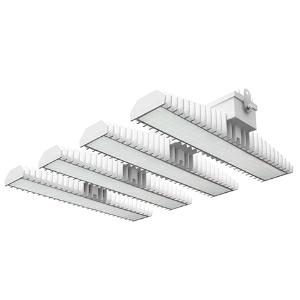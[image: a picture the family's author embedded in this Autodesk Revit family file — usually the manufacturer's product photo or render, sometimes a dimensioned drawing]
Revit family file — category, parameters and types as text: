
# Revit family: 3f_filippi_-_3f_lem_ht_medio_3f_filippi_-_59039_a0812_-_3f_lem_4_ht_led_120_cr_medio___vs_d09b
name_source: partatom
category: Lighting Fixtures
units: mm (PartAtom-declared; Revit-internal decimal feet)

## family parameters
Cut with Voids When Loaded = No
Host = Face
Light Source = No
Part Type = Normal
Room Calculation Point = No
Round Connector Dimension = Use Diameter
Shared = No

## types (1)
- 3F Filippi - 3F LEM HT Medio (1 x LED, 17236 lm, 136 W, 4000 K)
    Apparent Load = 136 VA
    Approval mark = ENEC
    CIE Flux Codes = 77 92 98 100 100
    Color Rendering = 80
    Color Temperature = 4000 K
    Control Gear = Electronic ballast
    Default Elevation = 1800 mm
    Description = Industrial luminaire with high light output and high luminous efficiency designed with the most innovative technologies for environments with temperature up to 70°C.

ILLUMINOTECHNICAL
Luminous efficiency 100% (DLOR 98%, ULOR 2%).
Initial luminous flux of the luminaire 17236 lm.
Medium distribution with rectangular shape.
Installation Interdistance Transv.D = 0.87 x hu - Long.D = 0.87 x hu.
Tabular UGR (CIE 117 - 4H-8H; S=0.25H; 70/50/20): RUG 19.7 - 19.7.
Beam angle: 58° - 57°.
Luminous efficacy 127 lm/W.
Lifetime (L93/B10): 30000 h. (tq+25°C)
Lifetime (L90/B10): 50000 h. (tq+25°C)
Lifetime (L85/B10): 80000 h. (tq+25°C)
Lifetime (L80/B10): 100000 h. (tq+25°C)
Lifetime (L85/B10): 50000 h. (tq+70°C)
Sudden decreased luminous flux after 50000 hours: 0% (C0).
Photobiological safety in compliance with IEC/TR 62778: RG0 risk exempt, (IEC 62471).
In compliance with IEC/EN 62722-2-1 - IEC/EN 62717 standards.
Luminous flux at +70°C: -13.5%.

SOURCE
4 Mid-Power linear LED modules 30W/840.
Energy efficiency class (UE 2019/2020 - UE 2019/2015): C.
CIE 13.3 Colour rendering index: CRI >80 (R9 <50%).
IES TM-30 Fidelity Index: Rf = 84 Rg = 95.
CCT nominal colour temperature 4000 K.
Colour initial tolerance (MacAdam): SDCM 3.

MECHANICAL
Passive modular heatsinks in die-casted aluminium, painted in white colour.
To optimize the thermal management of the LED module, the heatsinks are oversized and provided with self-cleaning of cooling fins.
Wiring body in aluminium and galvanised steel anchored solidly to the sinks and thermally separated.
3F Lens lenses with high luminous efficiency, transparent polycarbonate, fixed to the LED modules.
Fixing brackets in stainless steel.
Luminaire with limited surface temperature. - D - (EN 60598-2-24)
Dimensions: 757x542 mm, height 133 mm. Weight 18.14 kg.
IP65 protection degree.
Mechanical strength to impacts IK08 (5 joule).
Glow-wire test resistance 850°C.

ELECTRICAL
Halogen Free electronic wiring 230V-50/60Hz, power factor 0.97, THD <25%, constant output current, class I, 2 driver.
Power of the luminaire 136 W.
CE - IEC 60598-1 - EN 60598-1.
SAFE FLICKER: PstLM=<1 and SVM=<0.4 (IEC TR 61547-1 and IEC TR 63158), to ensure a more comfortable and safe light.
Luminaire compliant with EN 60598-2-22 for power supply from a centralised emergency system CPSS (Central Power Supply System), not incorporated in the luminaire - high risk areas excluded. The default power and flux are 100% in AC and 100% in DC.
Ambient temperature from -30°C to +70°C.
Temperature class T6 max 85°C.
Quick connection via M20 3P connector with 9-13 mm tightening range.
Power unit positioned on a separate compartment by the LED module to ensure optimum temperatures of cabling components, to be inspectable and maintainable.
Relative humidity UR: <85%.

INSTALLATION
Ceiling / Suspended / Wall.
All accessories dedicated to this product are available on the Catalog and on our website www.3F-Filippi.com.

ACCESSORIES
A0812 - Anti-glare microprismatic VS moulded glass, tempered, not flammable, with sealing gasket.
One required for each light module. The pack contains 10 pieces.

APPLICATIONS
In commercial environments, exhibition and industrial areas, stores, open areas.
Applications with high ambient temperature up to 70°C.

WARNING
Fixture not suitable for cold stores with an ambient temperature <0°C and/or relative humidity >85%.
Luminaire designed for disposal/recycling at end-of-life.
Replaceable (LED only) light source by a professional. Replaceable control gear by a professional.
    Height = 133 mm  [stored 0.436352 ft]
    Lamp = 1 x LED
    Lamp Light Flux = 17236 lm
    Lamp Power = 136 W
    Lamp count = 1
    Length = 757 mm
    Lifetime = 50000 h
    Luminous efficacy = 127 lm/W
    Manufacturer = 3F Filippi
    ModVariant = No
    Model = 3F Filippi - 59039+A0812 - 3F LEM 4 HT LED 120 CR MEDIO + VS
    Mounting Place = Ceiling
    Mounting Type = Pendant
    Number of Poles = 1
    OnlyDefault = Yes
    Power Factor = 1
    Product Name = 3F Filippi - 3F LEM HT Medio
    Product group = pendant luminaire
    ProductGroupID = 9
    Protection Class = Protection class I
    Protection Degree = IP 65
    RLX_Detail_Level = 1
    RLX_Emergency_Light_Flux = 0 lm
    RLX_Emergency_Type = 0
    RLX_Emergency_Type_DB = No
    RlxData = <blob elided: 119577 chars, md5=14e9faf6>
    Socket = socket
    Standby Power = 0 W
    System Light Flux = 17236 lm
    System Power = 136 W
    Type Comments = Product without accessories
    Type Image = 3f_filippi_-_lem_4__a0812.jpg
    URL = http://relux.com
    VarID = ---
    Voltage = 0 V
    Weight = 0.00 kg
    Width = 542 mm

note: [stored X ft] marks values corroborated as IEEE doubles in the binary element streams (Revit-internal decimal feet)

## geometry (parser evidence)
native form markers: Blend x4, Sweep x13
no freeform markers — native parametric forms only
